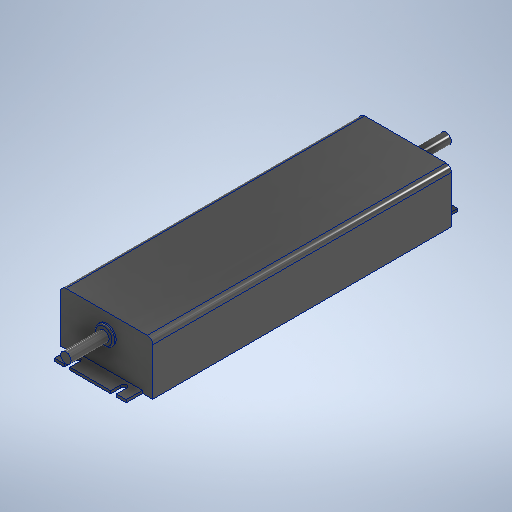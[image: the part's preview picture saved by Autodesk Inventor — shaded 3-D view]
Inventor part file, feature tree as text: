
AUTODESK INVENTOR PART (.ipt)
format: ipt  version: 2025 (Build 290162000, 162)  size: 329,728 bytes
history: native  units: in
note: dims shown in document units (in); Inventor stores cm internally (conversion verified against a paired STEP export)
features: extrude x4, sketch x3, fillet x2, mirror x1
ambient origin geometry x8: Origin, YZ Plane, XZ Plane, XY Plane, X Axis, Y Axis, Z Axis, Center Point
bodies: Solid1 (feature_tree)
feature tree (10):
  extrude  "Extrusion1"  Depth=2.0866in
  extrude  "Extrusion2"  Depth=0.0827in
  fillet  "Fillet1"  Radius=0.3701in
  sketch  "Sketch3"  dims[d5=0.1654in d6=0.0787in d7=0.0in d8=8.6693in d9=2.6772in d10=1.5276in d11=0.0in d12=0.1575in d13=0.9646in d14=0.5591in d15=0.3071in d16=0.0787in d17=0.0in d18=1.1811in d19=0.0in d20=0.0394in]
  extrude  "Extrusion3"  Depth=0.0787in TaperAngle=0.0deg
  extrude  "Extrusion4"  Depth=8.6693in
  fillet  "Fillet2"  Radius=2.6772in
  mirror  "Mirror1"
  sketch  "Sketch1"  dims[d0=9.6142in d1=2.0866in]
  sketch  "Sketch2"  dims[d2=0.378in d3=0.0827in d4=0.3701in]
